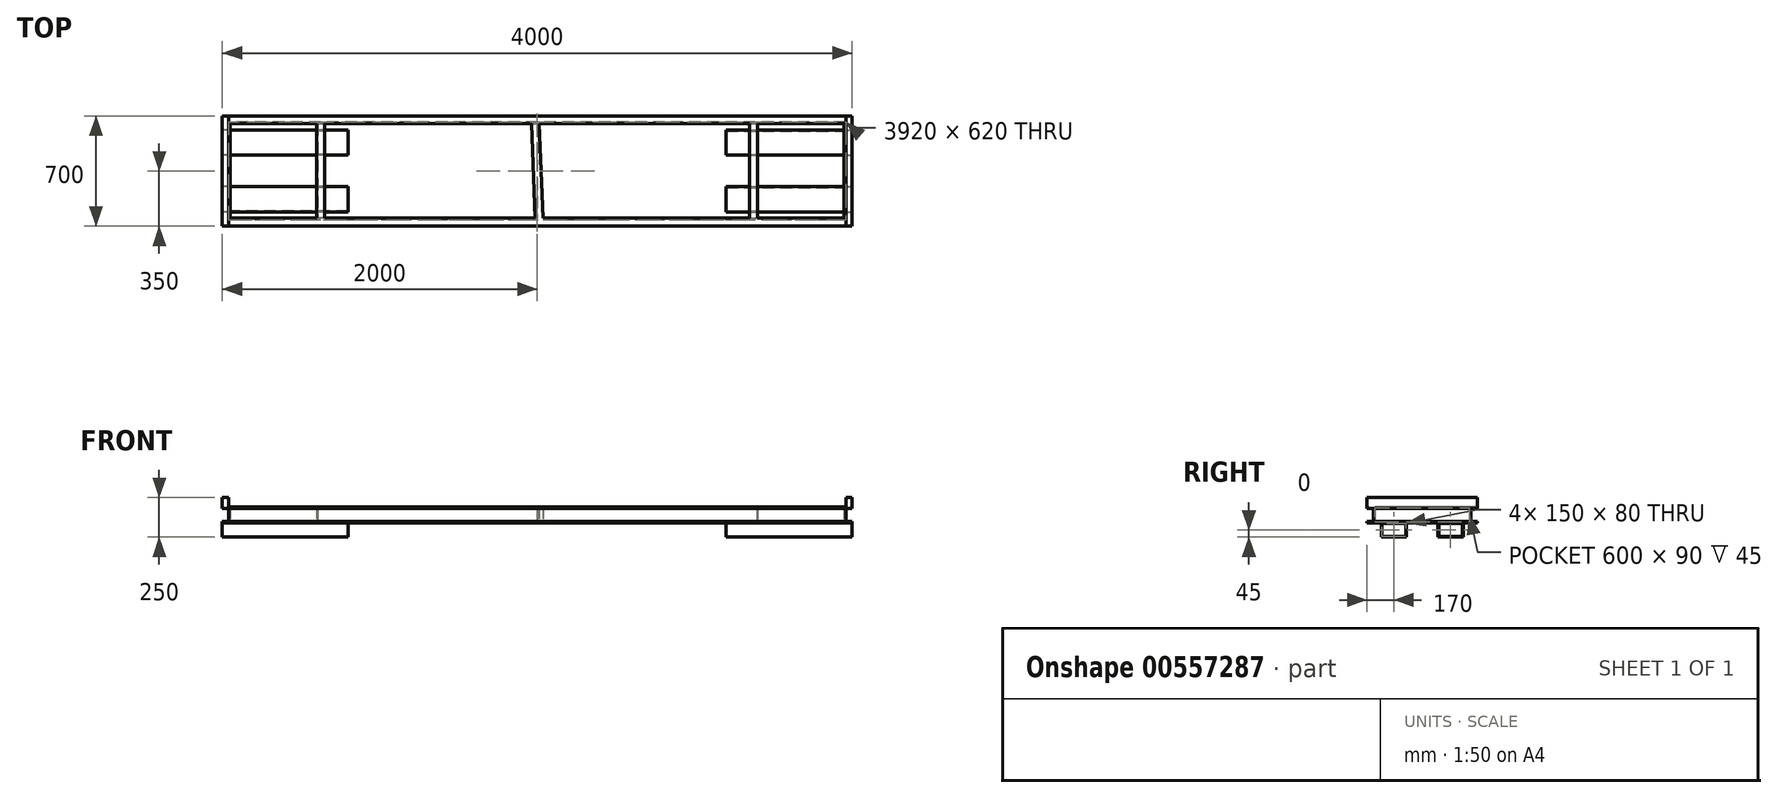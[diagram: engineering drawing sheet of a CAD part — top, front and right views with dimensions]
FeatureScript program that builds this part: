
annotation { "Feature Type Name" : "Feature", "Feature Type Description" : "" }
export const myFeature = defineFeature(function(context is Context, id is Id, definition is map)
    precondition{}
    {
        {
            var Q0;
            Q0=qCreatedBy(makeId("Top.planeOp"),FACE);
            var sketch = newSketch(context, id + "F0", { "sketchPlane" : qUnion([Q0])});
            skLineSegment(sketch, "E0.rect.bottom", {"start": v(2000, 350) * mm, "end": v(-2000, 350) * mm});
            skLineSegment(sketch, "E0.rect.top", {"start": v(2000, -350) * mm, "end": v(-2000, -350) * mm});
            skLineSegment(sketch, "E0.rect.left", {"start": v(2000, 350) * mm, "end": v(2000, -350) * mm});
            skLineSegment(sketch, "E0.rect.right", {"start": v(-2000, 350) * mm, "end": v(-2000, -350) * mm});
            skPoint(sketch, "E0.rect.middle", {"position": v(0, 0) * mm});
            skLineSegment(sketch, "E1.rect.bottom", {"start": v(1950, 300) * mm, "end": v(13.64, 300) * mm});
            skLineSegment(sketch, "E1.rect.top", {"start": v(1950, -300) * mm, "end": v(36.4, -300) * mm});
            skLineSegment(sketch, "E1.rect.left", {"start": v(1950, 300) * mm, "end": v(1950, -300) * mm});
            skLineSegment(sketch, "E1.rect.right", {"start": v(-1950, 300) * mm, "end": v(-1950, -300) * mm});
            skLineSegment(sketch, "E2.rect.left", {"start": v(13.64, 300) * mm, "end": v(36.4, -300) * mm});
            skLineSegment(sketch, "E2.rect.right", {"start": v(-36.4, 300) * mm, "end": v(-13.64, -300) * mm});
            skLineSegment(sketch, "E3.trimOffspring", {"start": v(-36.4, 300) * mm, "end": v(-1950, 300) * mm});
            skLineSegment(sketch, "E4.trimOffspring", {"start": v(-13.64, -300) * mm, "end": v(-1950, -300) * mm});
            skLineSegment(sketch, "E5", {"start": v(-1400, 300) * mm, "end": v(-1400, -300) * mm});
            skLineSegment(sketch, "E6", {"start": v(-1350, 300) * mm, "end": v(-1350, -300) * mm});
            skLineSegment(sketch, "E7", {"start": v(1400, 300) * mm, "end": v(1400, -300) * mm});
            skLineSegment(sketch, "E8", {"start": v(1350, 300) * mm, "end": v(1350, -300) * mm});
            skSolve(sketch);
        }
        {
            var Q0;
            Q0=makeQuery(id+"F0.imprint","IMPRINT",FACE,{"disambiguationData":[TD([[makeQuery(id+"F0.imprint","IMPRINT",EDGE,{"derivedFrom":sQuery(id+"F0.wireOp",EDGE,"E0.rect.bottom")}),1.0]])]});
            var Q1;
            {var subQ0=sQuery(id+"F0.wireOp",EDGE,"E5");Q1=makeQuery(id+"F0.imprint","IMPRINT",FACE,{"disambiguationData":[TD([[makeQuery(id+"F0.imprint","IMPRINT",EDGE,{"derivedFrom":subQ0}),1.0]])]});}
            var Q2;
            {var subQ0=sQuery(id+"F0.wireOp",EDGE,"E7");Q2=makeQuery(id+"F0.imprint","IMPRINT",FACE,{"disambiguationData":[TD([[makeQuery(id+"F0.imprint","IMPRINT",EDGE,{"derivedFrom":subQ0}),-1.0]])]});}
            extrude(context, id + "F1", {"entities" : qUnion([Q0, Q1, Q2]), "depth" : 100 * mm, "offsetDistance" : 25 * mm});
        }
        {
            var Q0;
            Q0=makeQuery(id+"F1.opExtrude","SWEPT_FACE",FACE,{"disambiguationData":[OSD([sQuery(id+"F0.wireOp",EDGE,"E0.rect.right")])]});
            var sketch = newSketch(context, id + "F2", { "sketchPlane" : qUnion([Q0])});
            skLineSegment(sketch, "E9.bottom", {"start": v(-350, 90) * mm, "end": v(-310, 90) * mm});
            skLineSegment(sketch, "E9.top", {"start": v(-350, 10) * mm, "end": v(-310, 10) * mm});
            skLineSegment(sketch, "E9.left", {"start": v(-350, 90) * mm, "end": v(-350, 10) * mm});
            skLineSegment(sketch, "E9.right", {"start": v(-310, 90) * mm, "end": v(-310, 10) * mm});
            skLineSegment(sketch, "E10.bottom", {"start": v(350, 90) * mm, "end": v(310, 90) * mm});
            skLineSegment(sketch, "E10.top", {"start": v(350, 10) * mm, "end": v(310, 10) * mm});
            skLineSegment(sketch, "E10.left", {"start": v(350, 90) * mm, "end": v(350, 10) * mm});
            skLineSegment(sketch, "E10.right", {"start": v(310, 90) * mm, "end": v(310, 10) * mm});
            skSolve(sketch);
        }
        {
            var Q0;
            Q0=makeQuery(id+"F2.imprint","IMPRINT",FACE,{"disambiguationData":[TD([[makeQuery(id+"F2.imprint","IMPRINT",EDGE,{"derivedFrom":sQuery(id+"F2.wireOp",EDGE,"E9.bottom")}),-1.0]])]});
            var Q1;
            Q1=makeQuery(id+"F2.imprint","IMPRINT",FACE,{"disambiguationData":[TD([[makeQuery(id+"F2.imprint","IMPRINT",EDGE,{"derivedFrom":sQuery(id+"F2.wireOp",EDGE,"E10.bottom")}),1.0]])]});
            extrude(context, id + "F3", {"entities" : qUnion([Q0, Q1]), "operationType" : NewBodyOperationType.REMOVE, "endBound" : BoundingType.THROUGH_ALL, "oppositeDirection" : true, "depth" : 25 * mm});
        }
        {
            var Q0;
            Q0=makeQuery(id+"F3.boolean.opBoolean","COPY",FACE,{"derivedFrom":makeQuery(id+"F3.opExtrude","SWEPT_FACE",FACE,{"disambiguationData":[OSD([sQuery(id+"F2.wireOp",EDGE,"E10.right")])]})});
            var sketch = newSketch(context, id + "F4", { "sketchPlane" : qUnion([Q0])});
            skLineSegment(sketch, "E11.bottom", {"start": v(2000, 90) * mm, "end": v(1960, 90) * mm});
            skLineSegment(sketch, "E11.top", {"start": v(2000, 10) * mm, "end": v(1960, 10) * mm});
            skLineSegment(sketch, "E11.left", {"start": v(2000, 90) * mm, "end": v(2000, 10) * mm});
            skLineSegment(sketch, "E11.right", {"start": v(1960, 90) * mm, "end": v(1960, 10) * mm});
            skLineSegment(sketch, "E12.bottom", {"start": v(-2000, 90) * mm, "end": v(-1960, 90) * mm});
            skLineSegment(sketch, "E12.top", {"start": v(-2000, 10) * mm, "end": v(-1960, 10) * mm});
            skLineSegment(sketch, "E12.left", {"start": v(-2000, 90) * mm, "end": v(-2000, 10) * mm});
            skLineSegment(sketch, "E12.right", {"start": v(-1960, 90) * mm, "end": v(-1960, 10) * mm});
            skSolve(sketch);
        }
        {
            var Q0;
            Q0=makeQuery(id+"F4.imprint","IMPRINT",FACE,{"disambiguationData":[TD([[makeQuery(id+"F4.imprint","IMPRINT",EDGE,{"derivedFrom":sQuery(id+"F4.wireOp",EDGE,"E11.bottom")}),1.0]])]});
            var Q1;
            Q1=makeQuery(id+"F4.imprint","IMPRINT",FACE,{"disambiguationData":[TD([[makeQuery(id+"F4.imprint","IMPRINT",EDGE,{"derivedFrom":sQuery(id+"F4.wireOp",EDGE,"E12.bottom")}),1.0]])]});
            extrude(context, id + "F5", {"entities" : qUnion([Q0, Q1]), "operationType" : NewBodyOperationType.REMOVE, "endBound" : BoundingType.THROUGH_ALL, "oppositeDirection" : true, "depth" : 25 * mm});
        }
        {
            var Q0;
            Q0=qCreatedBy(makeId("Front.planeOp"),FACE);
            var sketch = newSketch(context, id + "F6", { "sketchPlane" : qUnion([Q0])});
            skLineSegment(sketch, "E13.bottom", {"start": v(0, 10) * mm, "end": v(-90, 10) * mm});
            skLineSegment(sketch, "E13.top", {"start": v(0, 90) * mm, "end": v(-90, 90) * mm});
            skLineSegment(sketch, "E13.left", {"start": v(0, 10) * mm, "end": v(0, 90) * mm});
            skLineSegment(sketch, "E13.right", {"start": v(-90, 10) * mm, "end": v(-90, 90) * mm});
            skLineSegment(sketch, "E14.top", {"start": v(-1305, 95) * mm, "end": v(-1395, 95) * mm});
            skLineSegment(sketch, "E14.left", {"start": v(-1305, 5) * mm, "end": v(-1305, 95) * mm});
            skLineSegment(sketch, "E14.right", {"start": v(-1395, 5) * mm, "end": v(-1395, 95) * mm});
            skLineSegment(sketch, "E15.top", {"start": v(1395, 95) * mm, "end": v(1305, 95) * mm});
            skLineSegment(sketch, "E15.left", {"start": v(1395, 5) * mm, "end": v(1395, 95) * mm});
            skLineSegment(sketch, "E16", {"start": v(1395, 5) * mm, "end": v(1305, 5) * mm});
            skLineSegment(sketch, "E17", {"start": v(1305, 5) * mm, "end": v(1305, 95) * mm});
            skLineSegment(sketch, "E18", {"start": v(-1395, 5) * mm, "end": v(-1305, 5) * mm});
            skPoint(sketch, "E19.orphan", {"position": v(-1305, 0) * mm});
            skSolve(sketch);
        }
        {
            var Q0;
            Q0=qSketchRegion(id+"F6",true);
            var Q1;
            Q1=makeQuery(id+"F1.opExtrude","SWEPT_FACE",FACE,{"disambiguationData":[OSD([sQuery(id+"F0.wireOp",EDGE,"E3.trimOffspring")])]});
            var Q2;
            Q2=makeQuery(id+"F1.opExtrude","SWEPT_FACE",FACE,{"disambiguationData":[OSD([sQuery(id+"F0.wireOp",EDGE,"E4.trimOffspring")])]});
            extrude(context, id + "F7", {"entities" : qUnion([Q0]), "operationType" : NewBodyOperationType.REMOVE, "endBound" : BoundingType.UP_TO_SURFACE, "oppositeDirection" : true, "endBoundEntityFace" : qUnion([Q1]), "depth" : 25 * mm, "hasSecondDirection" : true, "secondDirectionBound" : SecondDirectionBoundingType.UP_TO_SURFACE, "secondDirectionOppositeDirection" : false, "secondDirectionBoundEntityFace" : qUnion([Q2]), "secondDirectionDepth" : 25 * mm});
        }
        {
            var Q0;
            Q0=makeQuery(id+"F1.opExtrude","CAP_FACE",FACE,{"disambiguationData":[OSD([sQuery(id+"F0.wireOp",EDGE,"E0.rect.bottom"),sQuery(id+"F0.wireOp",EDGE,"E0.rect.top"),sQuery(id+"F0.wireOp",EDGE,"E0.rect.left"),sQuery(id+"F0.wireOp",EDGE,"E0.rect.right"),sQuery(id+"F0.wireOp",EDGE,"E1.rect.bottom"),sQuery(id+"F0.wireOp",EDGE,"E1.rect.top"),sQuery(id+"F0.wireOp",EDGE,"E1.rect.left"),sQuery(id+"F0.wireOp",EDGE,"E1.rect.right"),sQuery(id+"F0.wireOp",EDGE,"E2.rect.left"),sQuery(id+"F0.wireOp",EDGE,"E2.rect.right"),sQuery(id+"F0.wireOp",EDGE,"E3.trimOffspring"),sQuery(id+"F0.wireOp",EDGE,"E4.trimOffspring")])],"isStart":false});
            var sketch = newSketch(context, id + "F8", { "sketchPlane" : qUnion([Q0])});
            skLineSegment(sketch, "E20.bottom", {"start": v(2000, 350) * mm, "end": v(1960, 350) * mm});
            skLineSegment(sketch, "E20.top", {"start": v(2000, -350) * mm, "end": v(1960, -350) * mm});
            skLineSegment(sketch, "E20.left", {"start": v(2000, 350) * mm, "end": v(2000, -350) * mm});
            skLineSegment(sketch, "E20.right", {"start": v(1960, 350) * mm, "end": v(1960, -350) * mm});
            skLineSegment(sketch, "E21.bottom", {"start": v(-2000, 350) * mm, "end": v(-1960, 350) * mm});
            skLineSegment(sketch, "E21.top", {"start": v(-2000, -350) * mm, "end": v(-1960, -350) * mm});
            skLineSegment(sketch, "E21.left", {"start": v(-2000, 350) * mm, "end": v(-2000, -350) * mm});
            skLineSegment(sketch, "E21.right", {"start": v(-1960, 350) * mm, "end": v(-1960, -350) * mm});
            skSolve(sketch);
        }
        {
            var Q0;
            Q0=makeQuery(id+"F8.imprint","IMPRINT",FACE,{"disambiguationData":[TD([[makeQuery(id+"F8.imprint","IMPRINT",EDGE,{"derivedFrom":sQuery(id+"F8.wireOp",EDGE,"E21.bottom")}),1.0]])]});
            var Q1;
            Q1=makeQuery(id+"F8.imprint","IMPRINT",FACE,{"disambiguationData":[TD([[makeQuery(id+"F8.imprint","IMPRINT",EDGE,{"derivedFrom":sQuery(id+"F8.wireOp",EDGE,"E20.bottom")}),1.0]])]});
            extrude(context, id + "F9", {"entities" : qUnion([Q0, Q1]), "operationType" : NewBodyOperationType.ADD, "depth" : 60 * mm});
        }
        {
            var Q0;
            {var subQ2=sQuery(id+"F0.wireOp",EDGE,"E0.rect.top");Q0=makeQuery(id+"F9.boolean.opBoolean","MERGE",FACE,{"derivedFrom":[makeQuery(id+"F3.boolean.opBoolean","SPLIT",FACE,{"disambiguationData":[TD([makeQuery(id+"F3.opExtrude","SWEPT_FACE",FACE,{"disambiguationData":[OSD([sQuery(id+"F2.wireOp",EDGE,"E10.bottom")])]})])],"derivedFrom":makeQuery(id+"F1.opExtrude","SWEPT_FACE",FACE,{"disambiguationData":[OSD([subQ2])]})}),makeQuery(id+"F9.opExtrude","SWEPT_FACE",FACE,{"disambiguationData":[OSD([sQuery(id+"F8.wireOp",EDGE,"E20.top")])]}),makeQuery(id+"F9.opExtrude","SWEPT_FACE",FACE,{"disambiguationData":[OSD([sQuery(id+"F8.wireOp",EDGE,"E21.top")])]})]});}
            var sketch = newSketch(context, id + "F10", { "sketchPlane" : qUnion([Q0])});
            skLineSegment(sketch, "E22.bottom", {"start": v(-1297.93, 157.5) * mm, "end": v(-1262.93, 157.5) * mm});
            skLineSegment(sketch, "E22.top", {"start": v(-1297.93, 102.5) * mm, "end": v(-1262.93, 102.5) * mm});
            skLineSegment(sketch, "E22.left", {"start": v(-1297.93, 157.5) * mm, "end": v(-1297.93, 102.5) * mm});
            skLineSegment(sketch, "E22.right", {"start": v(-1262.93, 157.5) * mm, "end": v(-1262.93, 102.5) * mm});
            skLineSegment(sketch, "E23.MirrorCS", {"start": v(1297.93, 157.5) * mm, "end": v(1297.93, 102.5) * mm});
            skLineSegment(sketch, "E24.MirrorCS", {"start": v(1297.93, 102.5) * mm, "end": v(1262.93, 102.5) * mm});
            skLineSegment(sketch, "E25.MirrorCS", {"start": v(1297.93, 157.5) * mm, "end": v(1262.93, 157.5) * mm});
            skLineSegment(sketch, "E26.MirrorCS", {"start": v(1262.93, 157.5) * mm, "end": v(1262.93, 102.5) * mm});
            skSolve(sketch);
        }
        {
            var Q0;
            Q0=makeQuery(id+"F10.imprint","IMPRINT",FACE,{"disambiguationData":[TD([[makeQuery(id+"F10.imprint","IMPRINT",EDGE,{"derivedFrom":sQuery(id+"F10.wireOp",EDGE,"E23.MirrorCS")}),-1.0]])]});
            var Q1;
            Q1=makeQuery(id+"F10.imprint","IMPRINT",FACE,{"disambiguationData":[TD([[makeQuery(id+"F10.imprint","IMPRINT",EDGE,{"derivedFrom":sQuery(id+"F10.wireOp",EDGE,"E22.bottom")}),-1.0]])]});
            extrude(context, id + "F11", {"entities" : qUnion([Q0, Q1]), "operationType" : NewBodyOperationType.REMOVE, "endBound" : BoundingType.THROUGH_ALL, "oppositeDirection" : true, "depth" : 25 * mm});
        }
        {
            var Q0;
            {var subQ1=sQuery(id+"F0.wireOp",EDGE,"E0.rect.right");Q0=makeQuery(id+"F5.boolean.opBoolean","SPLIT",FACE,{"disambiguationData":[TD([makeQuery(id+"F3.boolean.opBoolean","COPY",FACE,{"derivedFrom":makeQuery(id+"F3.opExtrude","SWEPT_FACE",FACE,{"disambiguationData":[OSD([sQuery(id+"F2.wireOp",EDGE,"E9.top")])]})})])],"derivedFrom":makeQuery(id+"F1.opExtrude","SWEPT_FACE",FACE,{"disambiguationData":[OSD([subQ1])]})});}
            var sketch = newSketch(context, id + "F12", { "sketchPlane" : qUnion([Q0])});
            skLineSegment(sketch, "E27.bottom", {"start": v(-260, 0) * mm, "end": v(-100, 0) * mm});
            skLineSegment(sketch, "E27.top", {"start": v(-260, -90) * mm, "end": v(-100, -90) * mm});
            skLineSegment(sketch, "E27.left", {"start": v(-260, 0) * mm, "end": v(-260, -90) * mm});
            skLineSegment(sketch, "E27.right", {"start": v(-100, 0) * mm, "end": v(-100, -90) * mm});
            skLineSegment(sketch, "E28.bottom", {"start": v(-255, -5) * mm, "end": v(-105, -5) * mm});
            skLineSegment(sketch, "E28.top", {"start": v(-255, -85) * mm, "end": v(-105, -85) * mm});
            skLineSegment(sketch, "E28.left", {"start": v(-255, -5) * mm, "end": v(-255, -85) * mm});
            skLineSegment(sketch, "E28.right", {"start": v(-105, -5) * mm, "end": v(-105, -85) * mm});
            skLineSegment(sketch, "E29.MirrorCS", {"start": v(100, 0) * mm, "end": v(100, -90) * mm});
            skLineSegment(sketch, "E30.MirrorCS", {"start": v(105, -5) * mm, "end": v(105, -85) * mm});
            skLineSegment(sketch, "E31.MirrorCS", {"start": v(255, -5) * mm, "end": v(105, -5) * mm});
            skLineSegment(sketch, "E32.MirrorCS", {"start": v(260, 0) * mm, "end": v(100, 0) * mm});
            skLineSegment(sketch, "E33.MirrorCS", {"start": v(255, -5) * mm, "end": v(255, -85) * mm});
            skLineSegment(sketch, "E34.MirrorCS", {"start": v(260, 0) * mm, "end": v(260, -90) * mm});
            skLineSegment(sketch, "E35.MirrorCS", {"start": v(255, -85) * mm, "end": v(105, -85) * mm});
            skLineSegment(sketch, "E36.MirrorCS", {"start": v(260, -90) * mm, "end": v(100, -90) * mm});
            skSolve(sketch);
        }
        {
            var Q0;
            Q0 = qSketchRegion(id + "F12", true);
            extrude(context, id + "F13", {"entities" : qUnion([Q0]), "oppositeDirection" : true, "depth" : 800 * mm, "offsetDistance" : 25 * mm});
        }
        {
            var Q0;
            Q0=makeQuery(id+"F13.opExtrude","SWEPT_BODY",BODY,{"disambiguationData":[OSD([sQuery(id+"F12.wireOp",EDGE,"E29.MirrorCS"),sQuery(id+"F12.wireOp",EDGE,"E30.MirrorCS"),sQuery(id+"F12.wireOp",EDGE,"E31.MirrorCS"),sQuery(id+"F12.wireOp",EDGE,"E32.MirrorCS"),sQuery(id+"F12.wireOp",EDGE,"E33.MirrorCS"),sQuery(id+"F12.wireOp",EDGE,"E34.MirrorCS"),sQuery(id+"F12.wireOp",EDGE,"E35.MirrorCS"),sQuery(id+"F12.wireOp",EDGE,"E36.MirrorCS")])]});
            var Q1;
            Q1=makeQuery(id+"F13.opExtrude","SWEPT_BODY",BODY,{"disambiguationData":[OSD([sQuery(id+"F12.wireOp",EDGE,"E27.bottom"),sQuery(id+"F12.wireOp",EDGE,"E27.top"),sQuery(id+"F12.wireOp",EDGE,"E27.left"),sQuery(id+"F12.wireOp",EDGE,"E27.right"),sQuery(id+"F12.wireOp",EDGE,"E28.bottom"),sQuery(id+"F12.wireOp",EDGE,"E28.top"),sQuery(id+"F12.wireOp",EDGE,"E28.left"),sQuery(id+"F12.wireOp",EDGE,"E28.right")])]});
            var Q2;
            Q2=qCreatedBy(makeId("Right.planeOp"),FACE);
            mirror(context, id + "F14", {"operationType" : NewBodyOperationType.ADD, "entities" : qUnion([Q0, Q1]), "mirrorPlane" : qUnion([Q2])});
        }
    });
